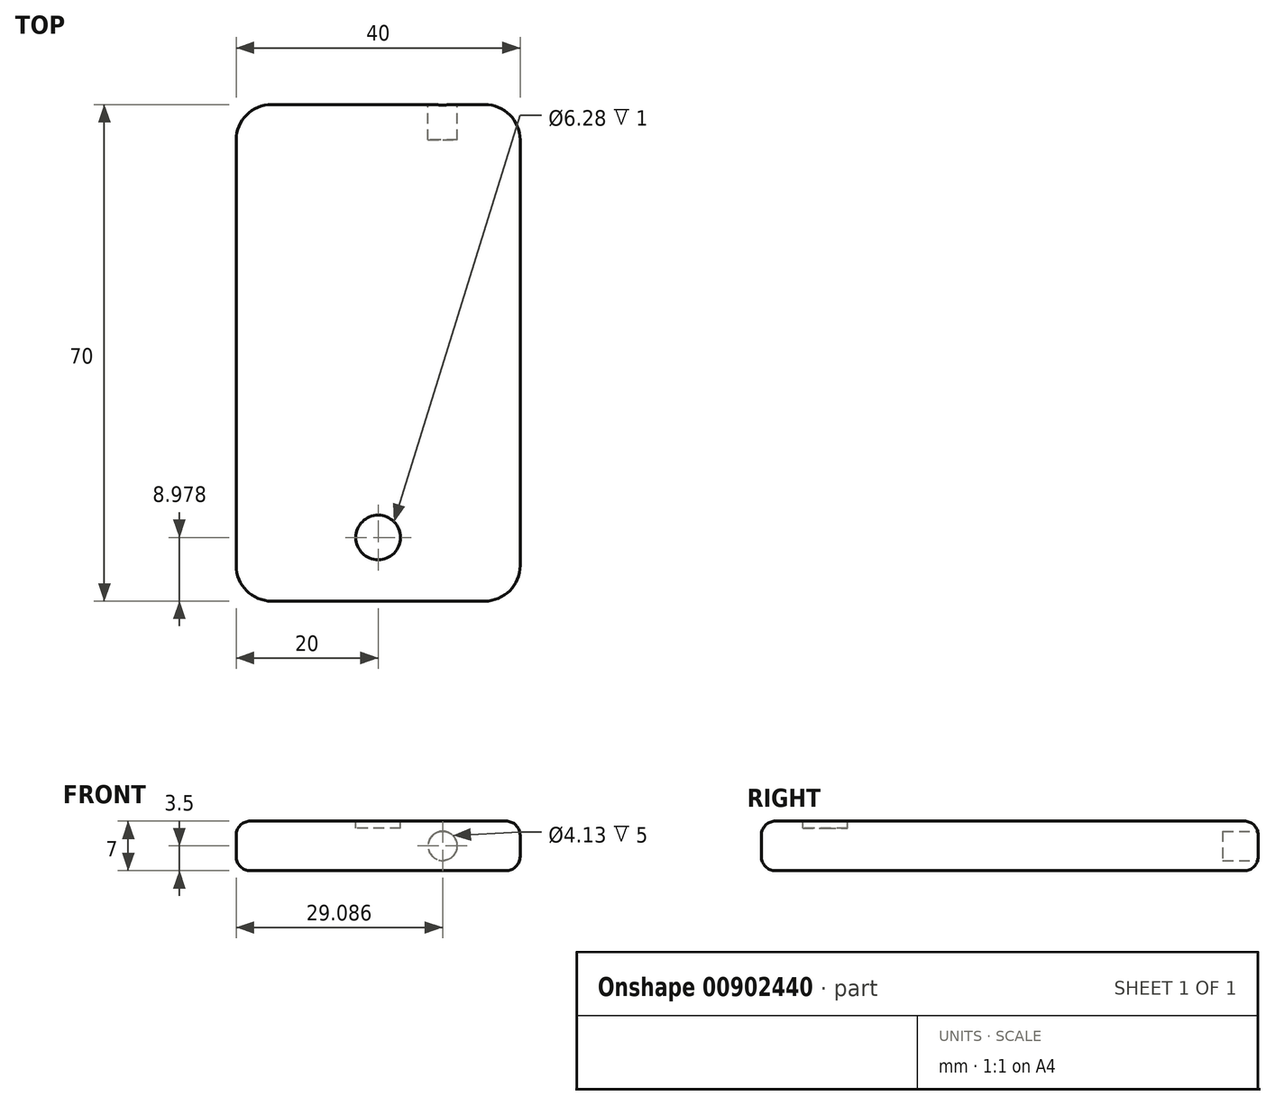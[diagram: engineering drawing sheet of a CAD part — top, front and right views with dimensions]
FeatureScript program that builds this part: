
annotation { "Feature Type Name" : "Feature", "Feature Type Description" : "" }
export const myFeature = defineFeature(function(context is Context, id is Id, definition is map)
    precondition{}
    {
        {
            var Q0;
            Q0=qCreatedBy(makeId("Top.planeOp"),FACE);
            var sketch = newSketch(context, id + "F0", { "sketchPlane" : qUnion([Q0])});
            skLineSegment(sketch, "E0.bottom", {"start": v(0, 70) * mm, "end": v(40, 70) * mm});
            skLineSegment(sketch, "E0.top", {"start": v(0, 0) * mm, "end": v(40, 0) * mm});
            skLineSegment(sketch, "E0.left", {"start": v(0, 70) * mm, "end": v(0, 0) * mm});
            skLineSegment(sketch, "E0.right", {"start": v(40, 70) * mm, "end": v(40, 0) * mm});
            skSolve(sketch);
        }
        {
            var Q0;
            Q0 = qSketchRegion(id + "F0", true);
            extrude(context, id + "F1", {"entities" : qUnion([Q0]), "depth" : 7 * mm, "offsetDistance" : 25 * mm});
        }
        {
            var Q0;
            Q0=makeQuery(id+"F1.opExtrude","SWEPT_EDGE",EDGE,{"disambiguationData":[OSD([sQuery(id+"F0.wireOp",EDGE,"E0.top"),sQuery(id+"F0.wireOp",EDGE,"E0.right")])]});
            var Q1;
            Q1=makeQuery(id+"F1.opExtrude","SWEPT_EDGE",EDGE,{"disambiguationData":[OSD([sQuery(id+"F0.wireOp",EDGE,"E0.bottom"),sQuery(id+"F0.wireOp",EDGE,"E0.right")])]});
            var Q2;
            Q2=makeQuery(id+"F1.opExtrude","SWEPT_EDGE",EDGE,{"disambiguationData":[OSD([sQuery(id+"F0.wireOp",EDGE,"E0.top"),sQuery(id+"F0.wireOp",EDGE,"E0.left")])]});
            var Q3;
            Q3=makeQuery(id+"F1.opExtrude","SWEPT_EDGE",EDGE,{"disambiguationData":[OSD([sQuery(id+"F0.wireOp",EDGE,"E0.bottom"),sQuery(id+"F0.wireOp",EDGE,"E0.left")])]});
            fillet(context, id + "F2", {"entities" : qUnion([Q0, Q1, Q2, Q3]), "radius" : 5 * mm, "tangentPropagation" : true, "allowEdgeOverflow" : false});
        }
        {
            var Q0;
            Q0=makeQuery(id+"F1.opExtrude","SWEPT_FACE",FACE,{"disambiguationData":[OSD([sQuery(id+"F0.wireOp",EDGE,"E0.bottom")])]});
            var sketch = newSketch(context, id + "F3", { "sketchPlane" : qUnion([Q0])});
            skCircle(sketch, "E1", {"center": v(-29.09, 3.5) * mm, "radius": 2.07 * mm});
            skPoint(sketch, "E1.centerSnap0", {"position": v(-35, 3.5) * mm});
            skSolve(sketch);
        }
        {
            var Q0;
            Q0=makeQuery(id+"F3.imprint","IMPRINT",FACE,{"disambiguationData":[TD([[makeQuery(id+"F3.imprint","IMPRINT",EDGE,{"derivedFrom":sQuery(id+"F3.wireOp",EDGE,"E1")}),1.0]])]});
            extrude(context, id + "F4", {"entities" : qUnion([Q0]), "operationType" : NewBodyOperationType.REMOVE, "oppositeDirection" : true, "depth" : 5 * mm, "offsetDistance" : 25 * mm});
        }
        {
            var Q0;
            Q0=makeQuery(id+"F1.opExtrude","CAP_EDGE",EDGE,{"disambiguationData":[OSD([sQuery(id+"F0.wireOp",EDGE,"E0.left")])],"isStart":false});
            var Q1;
            Q1=makeQuery(id+"F1.opExtrude","CAP_EDGE",EDGE,{"disambiguationData":[OSD([sQuery(id+"F0.wireOp",EDGE,"E0.left")])],"isStart":true});
            var Q2;
            Q2=makeQuery(id+"F1.opExtrude","CAP_EDGE",EDGE,{"disambiguationData":[OSD([sQuery(id+"F0.wireOp",EDGE,"E0.right")])],"isStart":true});
            fillet(context, id + "F5", {"entities" : qUnion([Q0, Q1, Q2]), "radius" : 2 * mm, "tangentPropagation" : true, "allowEdgeOverflow" : false});
        }
        {
            var Q0;
            Q0=makeQuery(id+"F1.opExtrude","CAP_FACE",FACE,{"disambiguationData":[OSD([sQuery(id+"F0.wireOp",EDGE,"E0.bottom"),sQuery(id+"F0.wireOp",EDGE,"E0.top"),sQuery(id+"F0.wireOp",EDGE,"E0.left"),sQuery(id+"F0.wireOp",EDGE,"E0.right")])],"isStart":false});
            var sketch = newSketch(context, id + "F6", { "sketchPlane" : qUnion([Q0])});
            skCircle(sketch, "E2", {"center": v(20, 8.98) * mm, "radius": 3.14 * mm});
            skPoint(sketch, "E2.centerSnap0", {"position": v(20, 2) * mm});
            skSolve(sketch);
        }
        {
            var Q0;
            Q0=makeQuery(id+"F6.imprint","IMPRINT",FACE,{"disambiguationData":[TD([[makeQuery(id+"F6.imprint","IMPRINT",EDGE,{"derivedFrom":sQuery(id+"F6.wireOp",EDGE,"E2")}),1.0]])]});
            var Q1;
            Q1=sQuery(id+"F6.wireOp",EDGE,"E2");
            extrude(context, id + "F7", {"entities" : qUnion([Q0]), "operationType" : NewBodyOperationType.REMOVE, "surfaceEntities" : qUnion([Q1]), "oppositeDirection" : true, "depth" : 1 * mm, "offsetDistance" : 25 * mm});
        }
    });
